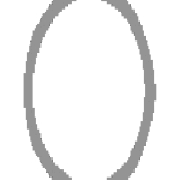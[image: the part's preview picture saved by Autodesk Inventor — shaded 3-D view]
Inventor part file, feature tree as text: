
AUTODESK INVENTOR PART (.ipt)
format: ipt  version: 2021 (Build 250183000, 183)  size: 110,080 bytes
history: native  units: in
note: dims shown in document units (in); Inventor stores cm internally (conversion verified against a paired STEP export)
features: other x4, sketch x3, plane x1
ambient origin geometry x8: Origin, YZ Plane, XZ Plane, XY Plane, X Axis, Y Axis, Z Axis, Center Point
bodies: Solid1 (feature_tree), Body (feature_tree)
feature tree (8):
  other  "Driven Length"
  other  "Frame Generator"
  other  "Start Plane"
  other  "End Plane"
  sketch  "Sketch"  dims[d2=13.0in d4=-0.0in d5=13.0in d6=0.12in d7=0.0in d8=90.0deg d9=13.0in]
  sketch  "Sketch2"  dims[d0=1.0in]
  plane  "Work Plane3"
  sketch  "Sketch3"  dims[d1=0.065in]
